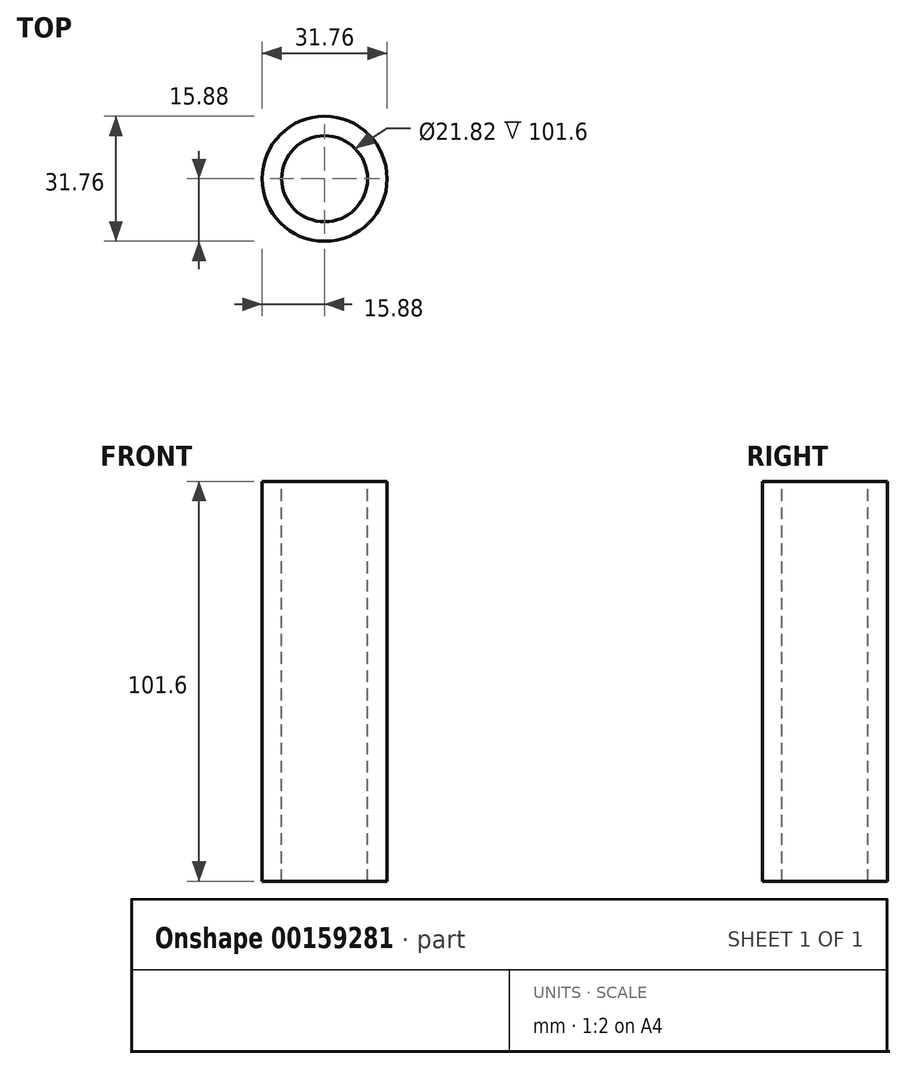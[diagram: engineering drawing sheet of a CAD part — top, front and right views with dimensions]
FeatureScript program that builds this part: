
annotation { "Feature Type Name" : "Feature", "Feature Type Description" : "" }
export const myFeature = defineFeature(function(context is Context, id is Id, definition is map)
    precondition{}
    {
        {
            var Q0;
            Q0=qCreatedBy(makeId("Top.planeOp"),FACE);
            var sketch = newSketch(context, id + "F0", { "sketchPlane" : qUnion([Q0])});
            skCircle(sketch, "E0", {"center": v(0, 0) * mm, "radius": 15.88 * mm});
            skSolve(sketch);
        }
        {
            var Q0;
            Q0=makeQuery(id+"F0.imprint","IMPRINT",FACE,{"disambiguationData":[TD([[makeQuery(id+"F0.imprint","IMPRINT",EDGE,{"derivedFrom":sQuery(id+"F0.wireOp",EDGE,"E0")}),1.0]])]});
            extrude(context, id + "F1", {"entities" : qUnion([Q0]), "endBound" : BoundingType.SYMMETRIC, "depth" : 101.6 * mm});
        }
        {
            var Q0;
            Q0=makeQuery(id+"F1.opExtrude","CAP_FACE",FACE,{"disambiguationData":[OSD([sQuery(id+"F0.wireOp",EDGE,"E0")])],"isStart":false});
            var sketch = newSketch(context, id + "F2", { "sketchPlane" : qUnion([Q0])});
            skCircle(sketch, "E1", {"center": v(0, 0) * mm, "radius": 10.91 * mm});
            skSolve(sketch);
        }
        {
            var Q0;
            Q0=makeQuery(id+"F2.imprint","IMPRINT",FACE,{"disambiguationData":[TD([[makeQuery(id+"F2.imprint","IMPRINT",EDGE,{"derivedFrom":sQuery(id+"F2.wireOp",EDGE,"E1")}),1.0]])]});
            extrude(context, id + "F3", {"entities" : qUnion([Q0]), "operationType" : NewBodyOperationType.REMOVE, "endBound" : BoundingType.THROUGH_ALL, "oppositeDirection" : true, "depth" : 25.4 * mm});
        }
    });
